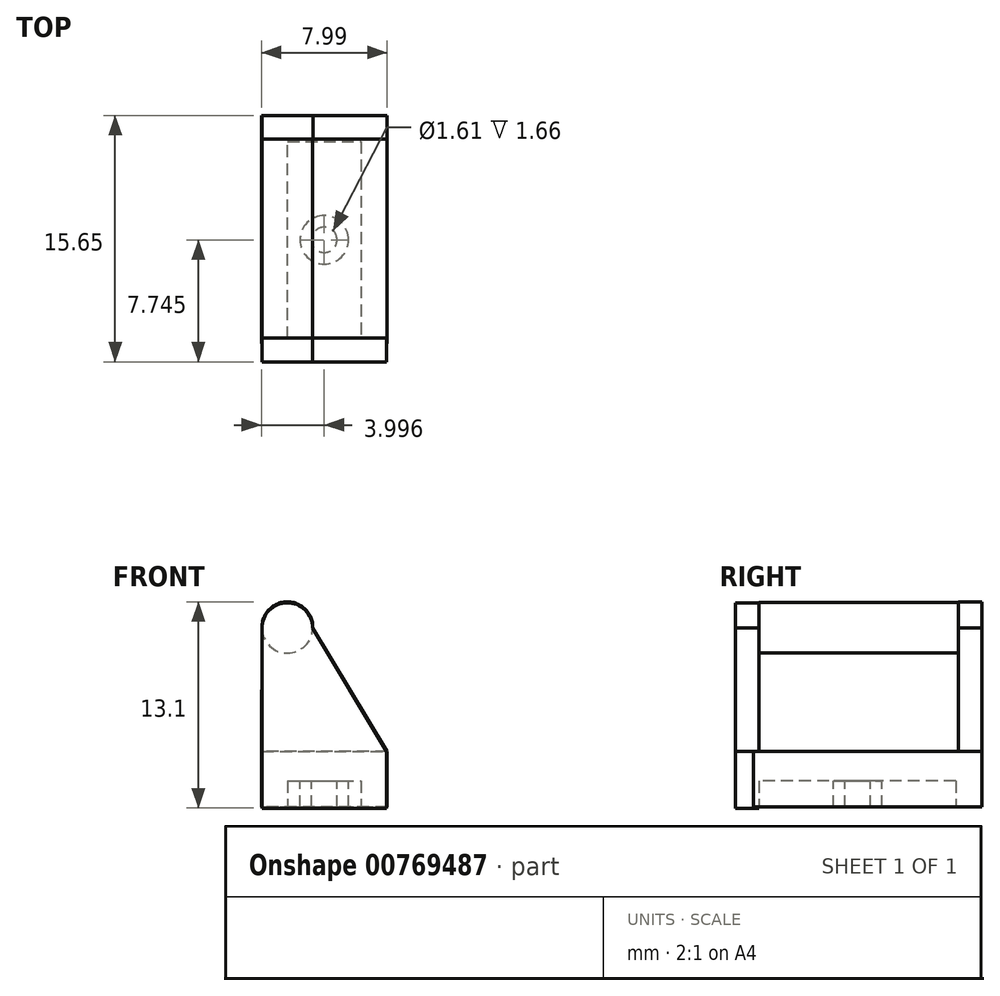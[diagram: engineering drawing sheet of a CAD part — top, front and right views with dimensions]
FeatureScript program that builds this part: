
annotation { "Feature Type Name" : "Feature", "Feature Type Description" : "" }
export const myFeature = defineFeature(function(context is Context, id is Id, definition is map)
    precondition{}
    {
        {
            var Q0;
            Q0=qCreatedBy(makeId("Front.planeOp"),FACE);
            var sketch = newSketch(context, id + "F0", { "sketchPlane" : qUnion([Q0])});
            skCircle(sketch, "E0", {"center": v(0, 0) * mm, "radius": 1.62 * mm});
            skSolve(sketch);
        }
        {
            var Q0;
            Q0 = qSketchRegion(id + "F0", true);
            extrude(context, id + "F1", {"entities" : qUnion([Q0]), "depth" : 12.65 * mm, "offsetDistance" : 25 * mm});
        }
        {
            var Q0;
            Q0=makeQuery(id+"F1.opExtrude","CAP_FACE",FACE,{"disambiguationData":[OSD([sQuery(id+"F0.wireOp",EDGE,"E0")])],"isStart":false});
            var sketch = newSketch(context, id + "F2", { "sketchPlane" : qUnion([Q0])});
            skLineSegment(sketch, "E1", {"start": v(-1.61, -0.03) * mm, "end": v(-1.61, -11.46) * mm});
            skLineSegment(sketch, "E2", {"start": v(-1.61, -11.46) * mm, "end": v(6.3, -11.46) * mm});
            skLineSegment(sketch, "E3", {"start": v(6.3, -11.46) * mm, "end": v(6.3, -7.84) * mm});
            skLineSegment(sketch, "E4", {"start": v(6.3, -7.84) * mm, "end": v(1.61, 0) * mm});
            skPoint(sketch, "E5.end.orphan", {"position": v(1.85, 0) * mm});
            skPoint(sketch, "E6", {"position": v(-1.61, -0.03) * mm});
            skPoint(sketch, "E7", {"position": v(1.61, 0) * mm});
            skArc(sketch, "E8", {"start": v(1.61, 0) * mm, "mid": v(-0.02, 1.58) * mm, "end": v(-1.61, -0.03) * mm});
            skSolve(sketch);
        }
        {
            var Q0;
            Q0 = qSketchRegion(id + "F2", true);
            extrude(context, id + "F3", {"entities" : qUnion([Q0]), "operationType" : NewBodyOperationType.ADD, "depth" : 1.5 * mm, "offsetDistance" : 25 * mm});
        }
        {
            var Q0;
            Q0=makeQuery(id+"F1.opExtrude","CAP_FACE",FACE,{"disambiguationData":[OSD([sQuery(id+"F0.wireOp",EDGE,"E0")])],"isStart":true});
            var sketch = newSketch(context, id + "F4", { "sketchPlane" : qUnion([Q0])});
            skArc(sketch, "E9", {"start": v(1.62, 0) * mm, "mid": v(0, 1.64) * mm, "end": v(-1.62, 0) * mm});
            skLineSegment(sketch, "E10", {"start": v(-1.62, 0) * mm, "end": v(-6.34, -7.85) * mm});
            skLineSegment(sketch, "E11", {"start": v(-6.34, -7.85) * mm, "end": v(-6.34, -11.39) * mm});
            skLineSegment(sketch, "E12", {"start": v(-6.34, -11.39) * mm, "end": v(1.65, -11.39) * mm});
            skLineSegment(sketch, "E13", {"start": v(1.65, -11.39) * mm, "end": v(1.62, 0) * mm});
            skSolve(sketch);
        }
        {
            var Q0;
            Q0 = qSketchRegion(id + "F4", true);
            extrude(context, id + "F5", {"entities" : qUnion([Q0]), "operationType" : NewBodyOperationType.ADD, "depth" : 1.5 * mm, "offsetDistance" : 25 * mm});
        }
        {
            var Q0;
            {var subQ0=sQuery(id+"F4.wireOp",EDGE,"E13");var subQ1=sQuery(id+"F4.wireOp",EDGE,"E12");var subQ2=sQuery(id+"F4.wireOp",EDGE,"E11");var subQ3=sQuery(id+"F4.wireOp",EDGE,"E10");var subQ4=sQuery(id+"F4.wireOp",EDGE,"E9");var subQ5=makeQuery(id+"F5.opExtrude","CAP_FACE",FACE,{"disambiguationData":[OSD([subQ4,subQ3,subQ2,subQ1,subQ0])],"isStart":true});Q0=makeQuery(id+"F5.boolean.opBoolean","SPLIT",FACE,{"disambiguationData":[TD([makeQuery(id+"F1.opExtrude","SWEPT_FACE",FACE,{"disambiguationData":[OSD([sQuery(id+"F0.wireOp",EDGE,"E0")])]}),makeQuery(id+"F5.opExtrude","SWEPT_FACE",FACE,{"disambiguationData":[OSD([subQ4])]}),subQ5,makeQuery(id+"F5.opExtrude","SWEPT_FACE",FACE,{"disambiguationData":[OSD([subQ3])]}),makeQuery(id+"F5.opExtrude","SWEPT_FACE",FACE,{"disambiguationData":[OSD([subQ2])]}),makeQuery(id+"F5.opExtrude","SWEPT_FACE",FACE,{"disambiguationData":[OSD([subQ1])]}),makeQuery(id+"F5.opExtrude","SWEPT_FACE",FACE,{"disambiguationData":[OSD([subQ0])]})])],"derivedFrom":subQ5});}
            var sketch = newSketch(context, id + "F6", { "sketchPlane" : qUnion([Q0])});
            skLineSegment(sketch, "E14", {"start": v(6.34, -11.39) * mm, "end": v(6.34, -7.85) * mm});
            skLineSegment(sketch, "E15", {"start": v(6.34, -7.85) * mm, "end": v(-1.64, -7.85) * mm});
            skLineSegment(sketch, "E16", {"start": v(-1.64, -7.85) * mm, "end": v(-1.65, -11.39) * mm});
            skLineSegment(sketch, "E17", {"start": v(-1.65, -11.39) * mm, "end": v(6.34, -11.39) * mm});
            skSolve(sketch);
        }
        {
            var Q0;
            Q0 = qSketchRegion(id + "F6", true);
            extrude(context, id + "F7", {"entities" : qUnion([Q0]), "operationType" : NewBodyOperationType.ADD, "depth" : 13 * mm, "offsetDistance" : 25 * mm});
        }
        {
            var Q0;
            Q0=makeQuery(id+"F7.boolean.opBoolean","MERGE",FACE,{"derivedFrom":[makeQuery(id+"F5.opExtrude","SWEPT_FACE",FACE,{"disambiguationData":[OSD([sQuery(id+"F4.wireOp",EDGE,"E12")])]}),makeQuery(id+"F7.opExtrude","SWEPT_FACE",FACE,{"disambiguationData":[OSD([sQuery(id+"F6.wireOp",EDGE,"E17")])]})]});
            var sketch = newSketch(context, id + "F8", { "sketchPlane" : qUnion([Q0])});
            skLineSegment(sketch, "E18.top", {"start": v(0.01, 0.16) * mm, "end": v(4.68, 0.16) * mm});
            skLineSegment(sketch, "E18.left", {"start": v(0.01, 12.65) * mm, "end": v(0.01, 0.16) * mm});
            skLineSegment(sketch, "E19", {"start": v(4.68, 0.16) * mm, "end": v(4.68, 12.65) * mm});
            skPoint(sketch, "E20.start.orphan", {"position": v(2.35, 12.96) * mm});
            skLineSegment(sketch, "E21", {"start": v(0.01, 12.65) * mm, "end": v(4.68, 12.65) * mm});
            skPoint(sketch, "E22.orphan", {"position": v(0.01, 12.96) * mm});
            skPoint(sketch, "E23.orphan", {"position": v(4.68, 12.96) * mm});
            skLineSegment(sketch, "E24", {"start": v(0.01, 12.5) * mm, "end": v(4.68, 12.5) * mm});
            skSolve(sketch);
        }
        {
            var Q0;
            Q0 = qSketchRegion(id + "F8", true);
            extrude(context, id + "F9", {"entities" : qUnion([Q0]), "operationType" : NewBodyOperationType.REMOVE, "oppositeDirection" : true, "depth" : 1.66 * mm, "offsetDistance" : 25 * mm});
        }
        {
            var Q0;
            Q0=makeQuery(id+"F9.boolean.opBoolean","COPY",FACE,{"derivedFrom":makeQuery(id+"F9.opExtrude","CAP_FACE",FACE,{"disambiguationData":[OSD([sQuery(id+"F8.wireOp",EDGE,"E18.top"),sQuery(id+"F8.wireOp",EDGE,"E18.left"),sQuery(id+"F8.wireOp",EDGE,"E19"),sQuery(id+"F8.wireOp",EDGE,"E21")])],"isStart":false})});
            var sketch = newSketch(context, id + "F10", { "sketchPlane" : qUnion([Q0])});
            skCircle(sketch, "E25", {"center": v(2.35, 6.4) * mm, "radius": 1.54 * mm});
            skPoint(sketch, "E25.centerSnap0", {"position": v(4.68, 6.4) * mm});
            skCircle(sketch, "E26", {"center": v(2.35, 6.4) * mm, "radius": 0.8 * mm});
            skSolve(sketch);
        }
        {
            var Q0;
            Q0 = qSketchRegion(id + "F10", true);
            extrude(context, id + "F11", {"entities" : qUnion([Q0]), "operationType" : NewBodyOperationType.ADD, "depth" : 1.66 * mm, "offsetDistance" : 25 * mm});
        }
    });
